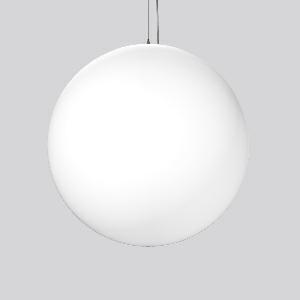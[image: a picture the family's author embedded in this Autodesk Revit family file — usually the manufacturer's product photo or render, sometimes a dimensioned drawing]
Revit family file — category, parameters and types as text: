
# Revit family: basic_ball_312114_002_76_4a17
name_source: partatom
category: Lighting Fixtures
units: mm (PartAtom-declared; Revit-internal decimal feet)

## family parameters
Cut with Voids When Loaded = No
Host = Face
Light Source = No
Part Type = Normal
Room Calculation Point = No
Round Connector Dimension = Use Diameter
Shared = No

## types (1)
- BASIC BALL (1 x LED Modul 930, 9350 lm, 3000)
    Apparent Load = 79 VA
    CIE Flux Codes = 25 50 75 54 100
    Color Rendering = 90
    Color Temperature = 3000
    Default Elevation = 1800 mm
    Description = Series: BASIC BALL
Pendant luminaire in timelessly classic sphere design. Canopy: metal, powder-coated, white. Metal cap: white, powder-coated. Diffuser: shockproof plastic (polyethylene), opal, satin finish. Shadow-free, homogeneous and soft illumination. Single-point steel cable suspension, steplessly adjustable. Special lengths available on request. Power supply cable: white. 
Colour: white
Diameter: 630 mm
Height: 630 mm
Suspension length: 300-4000 mm
Lamp: LED
Socket: without socket
Colour temperature: 3000K
Colour rendering index (CRI): 90
System power: 79 W
Rated luminous flux: 9350 lm
Luminous efficiency: 118 lm/W
Control gear: Converter, dimmable, DALI
Protection class: I
Type of protection: IP 40
    Height = 630 mm
    Lamp = 1 x LED Modul 930
    Lamp Light Flux = 9350 lm
    Lamp count = 1
    Length = 630 mm
    Lifetime = 50000 h
    Luminous efficacy = 118 lm/W
    Manufacturer = RZB
    ModVariant = No
    Model = 312114.002.76
    Mounting Place = Ceiling
    Mounting Type = Pendant
    Number of Poles = 1
    OnlyDefault = Yes
    Power Factor = 1
    Product Name = BASIC BALL
    Product group = Pendant luminaires
    ProductGroupID = 902
    Protection Class = Protection class I
    Protection Degree = IP 40
    RLX_Detail_Level = 1
    RLX_Emergency_Light_Flux = 0 lm
    RLX_Emergency_Type = 0
    RLX_Emergency_Type_DB = No
    RlxData = <blob elided: 122317 chars, md5=3e5c236a>
    Socket = socket
    Standby Power = 0 W
    System Light Flux = 9350 lm
    System Power = 79 W
    Type Comments = Product without accessories
    Type Image = 312108.002.jpg
    URL = http://relux.com
    VarID = ---
    Voltage = 230 V
    Voltage Range = 220-240 V
    Weight = 0.00 kg
    Width = 0 mm  [stored 0 ft]

note: [stored X ft] marks values corroborated as IEEE doubles in the binary element streams (Revit-internal decimal feet)

## geometry (parser evidence)
native form markers: Blend x4, Sweep x14
no freeform markers — native parametric forms only
